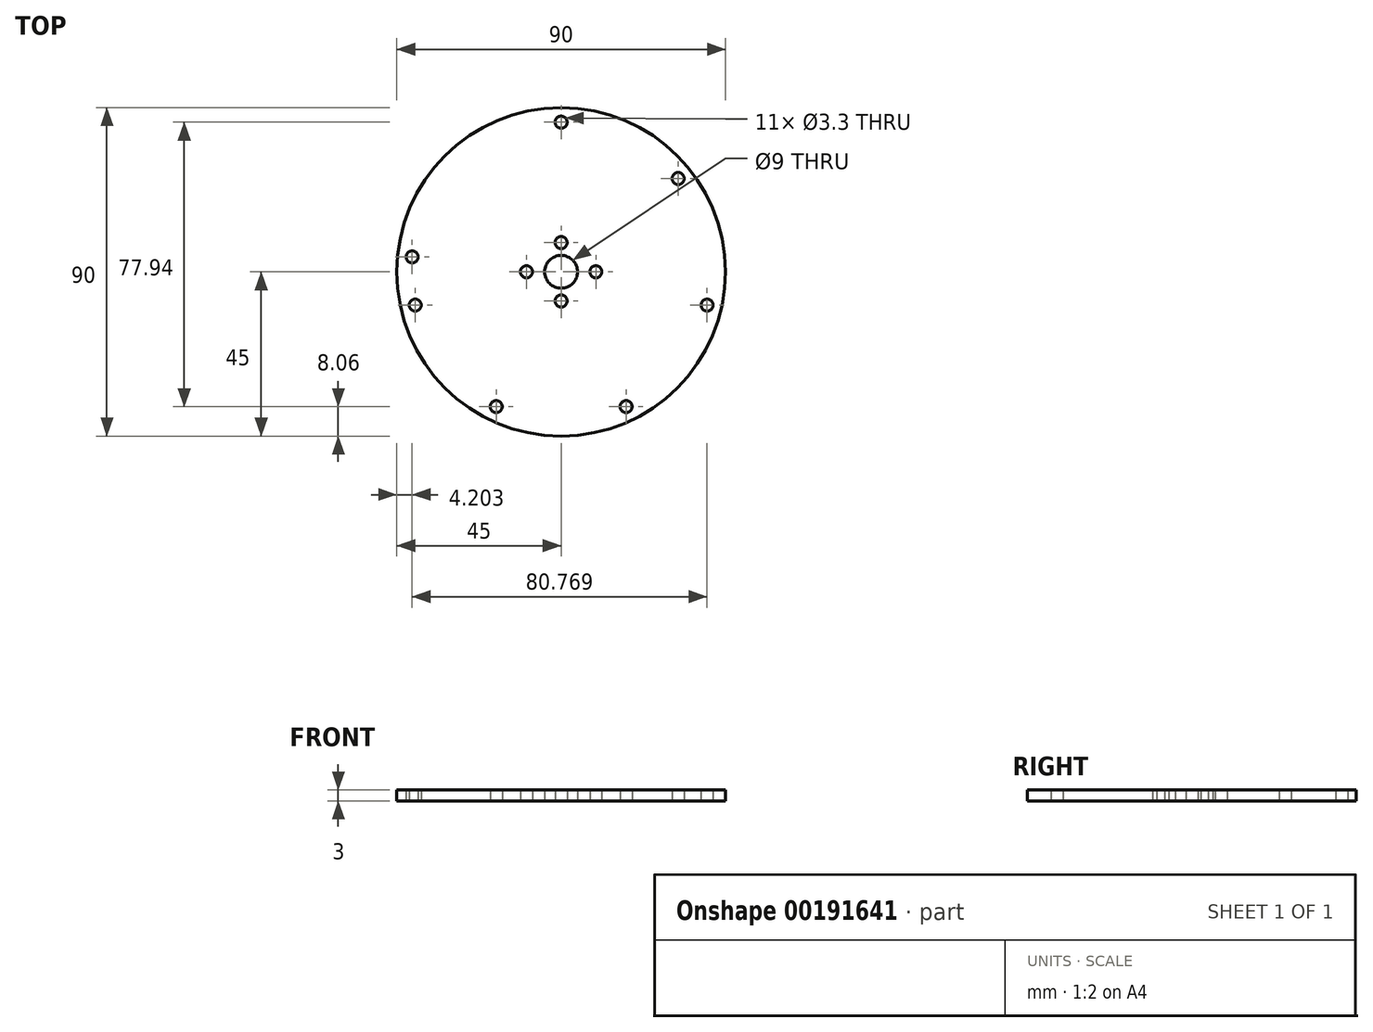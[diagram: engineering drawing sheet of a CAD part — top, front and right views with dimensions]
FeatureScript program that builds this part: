
annotation { "Feature Type Name" : "Feature", "Feature Type Description" : "" }
export const myFeature = defineFeature(function(context is Context, id is Id, definition is map)
    precondition{}
    {
        {
            var Q0;
            Q0=qCreatedBy(makeId("Top.planeOp"),FACE);
            var sketch = newSketch(context, id + "F0", { "sketchPlane" : qUnion([Q0])});
            skCircle(sketch, "E0", {"center": v(0, 0) * mm, "radius": 45 * mm});
            skCircle(sketch, "E1", {"center": v(0, 0) * mm, "radius": 41 * mm, "construction": true});
            skPoint(sketch, "E2", {"position": v(0, 41) * mm});
            skPoint(sketch, "E3.2.0", {"position": v(-39.97, -9.12) * mm});
            skPoint(sketch, "E3.3.0", {"position": v(-17.79, -36.94) * mm});
            skPoint(sketch, "E3.4.0", {"position": v(17.79, -36.94) * mm});
            skPoint(sketch, "E3.5.0", {"position": v(39.97, -9.12) * mm});
            skPoint(sketch, "E3.6.0", {"position": v(32.06, 25.56) * mm});
            skPoint(sketch, "E4", {"position": v(-40.8, 4.08) * mm});
            skCircle(sketch, "E5", {"center": v(0, 0) * mm, "radius": 9.5 * mm, "construction": true});
            skCircle(sketch, "E6", {"center": v(0, 0) * mm, "radius": 8 * mm, "construction": true});
            skCircle(sketch, "E7", {"center": v(0, 0) * mm, "radius": 4.5 * mm});
            skPoint(sketch, "E8", {"position": v(0, 8) * mm});
            skPoint(sketch, "E9", {"position": v(0, -8) * mm});
            skPoint(sketch, "E10", {"position": v(9.5, 0) * mm});
            skPoint(sketch, "E11", {"position": v(-9.5, 0) * mm});
            skSolve(sketch);
        }
        {
            var Q0;
            Q0=makeQuery(id+"F0.imprint","IMPRINT",FACE,{"disambiguationData":[TD([[makeQuery(id+"F0.imprint","IMPRINT",EDGE,{"derivedFrom":sQuery(id+"F0.wireOp",EDGE,"E0")}),1.0]])]});
            extrude(context, id + "F1", {"entities" : qUnion([Q0]), "depth" : 3 * mm, "offsetDistance" : 25 * mm});
        }
        {
            var Q0;
            Q0=sQuery(id+"F0.wireOp",VERTEX,"E10");
            var Q1;
            Q1=sQuery(id+"F0.wireOp",VERTEX,"E8");
            var Q2;
            Q2=sQuery(id+"F0.wireOp",VERTEX,"E11");
            var Q3;
            Q3=sQuery(id+"F0.wireOp",VERTEX,"E9");
            var Q4;
            Q4=sQuery(id+"F0.wireOp",VERTEX,"E3.6.0");
            var Q5;
            Q5=sQuery(id+"F0.wireOp",VERTEX,"E3.5.0");
            var Q6;
            Q6=sQuery(id+"F0.wireOp",VERTEX,"E3.4.0");
            var Q7;
            Q7=sQuery(id+"F0.wireOp",VERTEX,"E3.3.0");
            var Q8;
            Q8=sQuery(id+"F0.wireOp",VERTEX,"E3.2.0");
            var Q9;
            Q9=sQuery(id+"F0.wireOp",VERTEX,"E4");
            var Q10;
            Q10=sQuery(id+"F0.wireOp",VERTEX,"E2");
            var Q11;
            Q11=makeQuery(id+"F1.opExtrude","SWEPT_BODY",BODY,{"disambiguationData":[OSD([sQuery(id+"F0.wireOp",EDGE,"E0"),sQuery(id+"F0.wireOp",EDGE,"E7")])]});
            hole(context, id + "F2", {"style" : HoleStyle.SIMPLE, "endStyle" : HoleEndStyle.THROUGH, "oppositeDirection" : true, "standardTappedOrClearance" : lookupTablePath({ "standard" : "ISO", "fit" : "Normal", "size" : "M3", "type" : "Clearance" }), "standardBlindInLast" : lookupTablePath({ "fit" : "Standard", "standard" : "ISO", "size" : "M3", "type" : "Clearance" }), "holeDiameter" : 3.3 * mm, "majorDiameter" : 5 * mm, "isTappedThrough" : true, "tappedDepth" : 6.2 * mm, "tapClearance" : 3, "locations" : qUnion([Q0, Q1, Q2, Q3, Q4, Q5, Q6, Q7, Q8, Q9, Q10]), "scope" : qUnion([Q11])});
        }
    });
